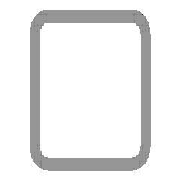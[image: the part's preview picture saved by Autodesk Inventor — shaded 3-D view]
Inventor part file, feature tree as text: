
AUTODESK INVENTOR PART (.ipt)
format: ipt  version: 2025 (Build 290162010, 162A)  size: 137,216 bytes
history: native  units: mm (DEFAULTED — no unit token found)
features: other x4, sketch x1, plane x1
ambient origin geometry x8: Origin, YZ Plane, XZ Plane, XY Plane, X Axis, Y Axis, Z Axis, Center Point
bodies: Solid1 (feature_tree), Body (feature_tree)
feature tree (6):
  parser-record x1  (decoder bookkeeping rows leaked as tree rows — omitted from the tree; the rows remain in map.json)
  other  "Driven Length"
  other  "Start Plane"
  other  "End Plane"
  sketch  "Sketch3"  dims[d3=1240.0mm d4=0.0mm d7=4.5mm d10=80.0mm d11=80.0mm d12=3.0mm d13=80.0mm d14=1320.0mm d15=40.0mm d16=40.0mm d17=90.0deg d18=1240.0mm]
  plane  "Work Plane3"
